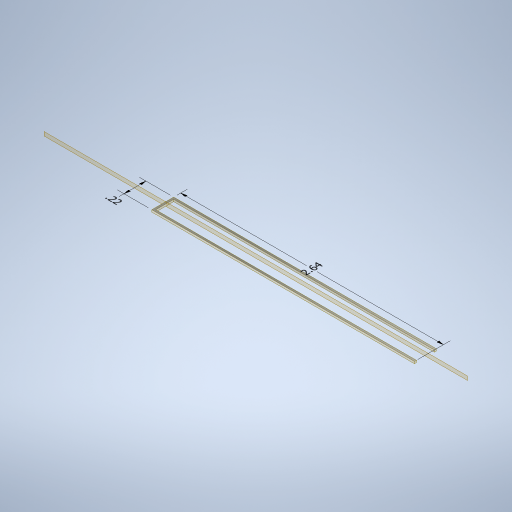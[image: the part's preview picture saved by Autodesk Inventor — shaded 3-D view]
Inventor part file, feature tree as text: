
AUTODESK INVENTOR PART (.ipt)
format: ipt  version: 2024.2 (Build 282272000, 272)  size: 278,016 bytes
history: native  units: in
note: dims shown in document units (in); Inventor stores cm internally (conversion verified against a paired STEP export)
features: other x3, plane x3, sketch x2, sweep x1
ambient origin geometry x8: Origin, YZ Plane, XZ Plane, XY Plane, X Axis, Y Axis, Z Axis, Center Point
bodies: Solid1 (feature_tree)
feature tree (9):
  other  "Annotations"
  sweep  "Sweep1"
  plane  "Work Plane1"
  plane  "Work Plane2"
  plane  "Work Plane4"
  sketch  "Sketch1"  dims[d6=0.0in d7=0.0in d11=0.25in d19=-0.25in]
  sketch  "Sketch2"  dims[d69=2.625in d70=2.625in d86=-0.1175in d89=0.2in d90=0.0in d91=0.0in d92=0.0in d98=0.02in d99=0.02in d100=0.1997in d101=2.635in d102=0.2692in d103=0.1197in d104=0.22in]
  other  "Linear Dimension 1"
  other  "Linear Dimension 2"
